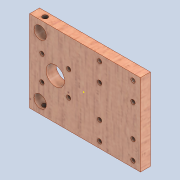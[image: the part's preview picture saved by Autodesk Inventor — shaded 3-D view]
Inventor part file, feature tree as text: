
AUTODESK INVENTOR PART (.ipt)
format: ipt  version: 2020 (Build 240168000, 168)  size: 297,472 bytes
history: native  units: mm
features: sketch x7, other x6, extrude x4, hole x3, pattern_linear x2, reference x2, direct_edit x1, move_body x1
ambient origin geometry x8: Origin, YZ Plane, XZ Plane, XY Plane, X Axis, Y Axis, Z Axis, Center Point
bodies: Solid1 (feature_tree)
feature tree (26):
  extrude  "Extrusion1"  Depth=66.0mm
  extrude  "Extrusion4"  TaperAngle=0.0deg  [1 undecoded]
  extrude  "Extrusion5"  TaperAngle=0.0deg  [1 undecoded]
  extrude  "Extrusion6"  Depth=9.0mm
  sketch  "Sketch7"  dims[d27=8.5mm d28=9.0mm]
  hole  "Hole1"  [1 undecoded]
  direct_edit  "Direct Edit1"
  pattern_linear  "Rectangular Pattern2"  Spacing1=3.5mm  [1 undecoded]
  pattern_linear  "Rectangular Pattern3"  Spacing1=21.5mm  [1 undecoded]
  hole  "Hole2"  [1 undecoded]
  hole  "Hole3"  [1 undecoded]
  sketch  "Sketch1"  dims[d0=87.5mm d1=66.0mm]
  sketch  "Sketch4"  dims[d2=8.0mm d3=0.0mm d19=0.0mm d20=0.0mm]
  sketch  "Sketch6"  dims[d24=15.0mm d25=0.0mm d26=0.0mm]
  sketch  "Sketch8"  dims[d29=10.0mm d30=9.0mm]
  reference  "Reference7"
  reference  "Reference8"
  sketch  "Sketch10"  dims[d31=0.0mm d32=0.0mm]
  sketch  "Sketch11"  dims[d33=20.748842mm d35=3.5mm d36=21.5mm d37=20.0mm d38=4.0mm d39=5.0mm d40=15.0mm d41=5.0mm d42=15.0mm d43=3.5mm d44=6.0mm d45=4.0mm d46=2.0mm d47=90.0deg d48=8.0mm d49=20.594885mm d53=0.0mm d54=0.0mm d55=2.0mm d56=26.0mm d57=20.0mm d59=15.0mm d60=20.0mm d62=41.0mm d63=20.0mm d65=27.0mm d66=8.5mm d67=4.134mm d68=5.0mm d69=4.0mm d70=2.0mm d71=90.0deg d72=7.45mm d73=20.594885mm d74=8.5mm d75=4.134mm d76=5.0mm d77=4.0mm d78=2.0mm d79=90.0deg d80=7.45mm d81=20.594885mm]
  parser-record x1  (decoder bookkeeping rows leaked as tree rows — omitted from the tree; the rows remain in map.json)
  other  "0005-00-00 Ansamblu_General.iam"
  other  "Surub M4 saiba piulita.iam:65"
  other  "0005-10-1013 ISO 7089 - 4 - 140 HV.ipt:2"
  move_body  "Move1"
  other  "0005-10-04 Z axis and extruder.iam"
  other  "0005-10-1002  Hub.ipt:22"
note: 7 required parameter values undecoded (feature->parameter linkage not recoverable at this tier; creation-order binding heuristic only, values carry confidence <= 0.55)
note: 1 file-system path scrubbed to <path> (originals preserved in map.json)
